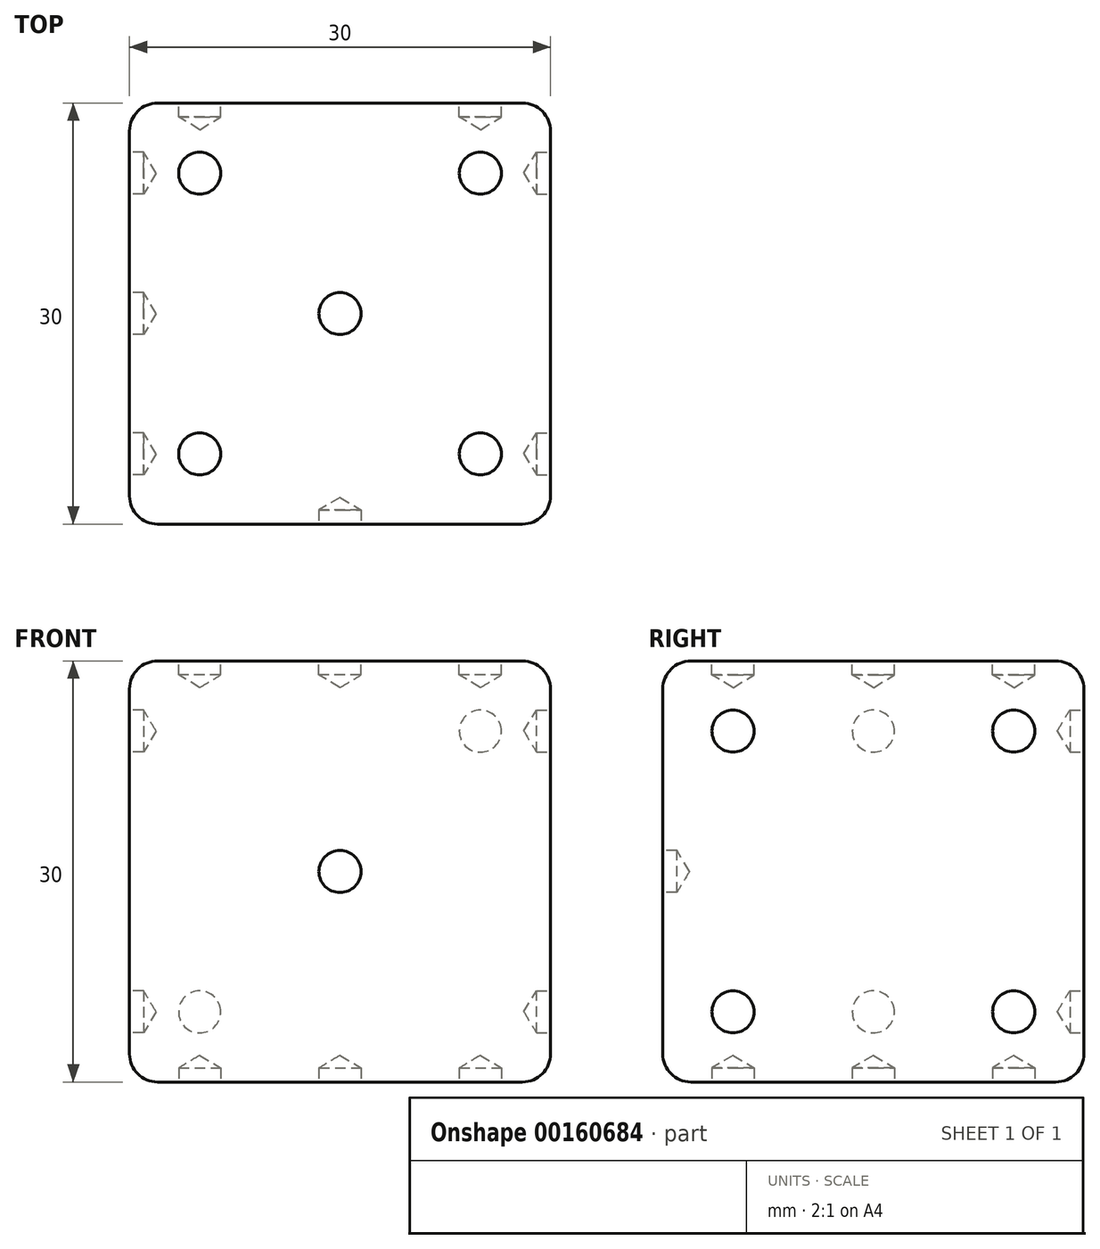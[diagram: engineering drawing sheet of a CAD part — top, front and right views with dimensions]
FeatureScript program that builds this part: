
annotation { "Feature Type Name" : "Feature", "Feature Type Description" : "" }
export const myFeature = defineFeature(function(context is Context, id is Id, definition is map)
    precondition{}
    {
        {
            var Q0;
            Q0=qCreatedBy(makeId("Front.planeOp"),FACE);
            var sketch = newSketch(context, id + "F0", { "sketchPlane" : qUnion([Q0])});
            skLineSegment(sketch, "E0.bottom", {"start": v(15, -15) * mm, "end": v(-15, -15) * mm});
            skLineSegment(sketch, "E0.top", {"start": v(15, 15) * mm, "end": v(-15, 15) * mm});
            skLineSegment(sketch, "E0.left", {"start": v(15, -15) * mm, "end": v(15, 15) * mm});
            skLineSegment(sketch, "E0.right", {"start": v(-15, -15) * mm, "end": v(-15, 15) * mm});
            skPoint(sketch, "E0.middle", {"position": v(0, 0) * mm});
            skSolve(sketch);
        }
        {
            var Q0;
            Q0=makeQuery(id+"F0.imprint","IMPRINT",FACE,{"disambiguationData":[TD([[makeQuery(id+"F0.imprint","IMPRINT",EDGE,{"derivedFrom":sQuery(id+"F0.wireOp",EDGE,"E0.bottom")}),-1.0]])]});
            extrude(context, id + "F1", {"entities" : qUnion([Q0]), "endBound" : BoundingType.SYMMETRIC, "depth" : 30 * mm});
        }
        {
            var Q0;
            Q0=makeQuery(id+"F1.opExtrude","CAP_EDGE",EDGE,{"disambiguationData":[OSD([sQuery(id+"F0.wireOp",EDGE,"E0.top")])],"isStart":false});
            var Q1;
            Q1=makeQuery(id+"F1.opExtrude","CAP_EDGE",EDGE,{"disambiguationData":[OSD([sQuery(id+"F0.wireOp",EDGE,"E0.left")])],"isStart":false});
            var Q2;
            Q2=makeQuery(id+"F1.opExtrude","SWEPT_EDGE",EDGE,{"disambiguationData":[OSD([sQuery(id+"F0.wireOp",EDGE,"E0.top"),sQuery(id+"F0.wireOp",EDGE,"E0.left")])]});
            var Q3;
            Q3=makeQuery(id+"F1.opExtrude","CAP_EDGE",EDGE,{"disambiguationData":[OSD([sQuery(id+"F0.wireOp",EDGE,"E0.top")])],"isStart":true});
            var Q4;
            Q4=makeQuery(id+"F1.opExtrude","SWEPT_EDGE",EDGE,{"disambiguationData":[OSD([sQuery(id+"F0.wireOp",EDGE,"E0.top"),sQuery(id+"F0.wireOp",EDGE,"E0.right")])]});
            var Q5;
            Q5=makeQuery(id+"F1.opExtrude","CAP_EDGE",EDGE,{"disambiguationData":[OSD([sQuery(id+"F0.wireOp",EDGE,"E0.left")])],"isStart":true});
            var Q6;
            Q6=makeQuery(id+"F1.opExtrude","SWEPT_EDGE",EDGE,{"disambiguationData":[OSD([sQuery(id+"F0.wireOp",EDGE,"E0.bottom"),sQuery(id+"F0.wireOp",EDGE,"E0.left")])]});
            var Q7;
            Q7=makeQuery(id+"F1.opExtrude","CAP_EDGE",EDGE,{"disambiguationData":[OSD([sQuery(id+"F0.wireOp",EDGE,"E0.bottom")])],"isStart":false});
            var Q8;
            Q8=makeQuery(id+"F1.opExtrude","CAP_EDGE",EDGE,{"disambiguationData":[OSD([sQuery(id+"F0.wireOp",EDGE,"E0.right")])],"isStart":false});
            var Q9;
            Q9=makeQuery(id+"F1.opExtrude","CAP_EDGE",EDGE,{"disambiguationData":[OSD([sQuery(id+"F0.wireOp",EDGE,"E0.right")])],"isStart":true});
            var Q10;
            Q10=makeQuery(id+"F1.opExtrude","SWEPT_EDGE",EDGE,{"disambiguationData":[OSD([sQuery(id+"F0.wireOp",EDGE,"E0.bottom"),sQuery(id+"F0.wireOp",EDGE,"E0.right")])]});
            var Q11;
            Q11=makeQuery(id+"F1.opExtrude","CAP_EDGE",EDGE,{"disambiguationData":[OSD([sQuery(id+"F0.wireOp",EDGE,"E0.bottom")])],"isStart":true});
            fillet(context, id + "F2", {"entities" : qUnion([Q0, Q1, Q2, Q3, Q4, Q5, Q6, Q7, Q8, Q9, Q10, Q11]), "radius" : 2 * mm, "tangentPropagation" : true, "allowEdgeOverflow" : false});
        }
        {
            var Q0;
            Q0=makeQuery(id+"F1.opExtrude","CAP_FACE",FACE,{"disambiguationData":[OSD([sQuery(id+"F0.wireOp",EDGE,"E0.bottom"),sQuery(id+"F0.wireOp",EDGE,"E0.top"),sQuery(id+"F0.wireOp",EDGE,"E0.left"),sQuery(id+"F0.wireOp",EDGE,"E0.right")])],"isStart":false});
            var sketch = newSketch(context, id + "F3", { "sketchPlane" : qUnion([Q0])});
            skPoint(sketch, "E1", {"position": v(0, 0) * mm});
            skSolve(sketch);
        }
        {
            var Q0;
            Q0=makeQuery(id+"F1.opExtrude","SWEPT_FACE",FACE,{"disambiguationData":[OSD([sQuery(id+"F0.wireOp",EDGE,"E0.bottom")])]});
            var sketch = newSketch(context, id + "F4", { "sketchPlane" : qUnion([Q0])});
            skPoint(sketch, "E2", {"position": v(10, 10) * mm});
            skPoint(sketch, "E3", {"position": v(0, 0) * mm});
            skPoint(sketch, "E4", {"position": v(-10, -10) * mm});
            skSolve(sketch);
        }
        {
            var Q0;
            Q0=makeQuery(id+"F1.opExtrude","SWEPT_FACE",FACE,{"disambiguationData":[OSD([sQuery(id+"F0.wireOp",EDGE,"E0.left")])]});
            var sketch = newSketch(context, id + "F5", { "sketchPlane" : qUnion([Q0])});
            skPoint(sketch, "E5", {"position": v(-10, 10) * mm});
            skPoint(sketch, "E6", {"position": v(-10, -10) * mm});
            skPoint(sketch, "E7", {"position": v(10, -10) * mm});
            skPoint(sketch, "E8", {"position": v(10, 10) * mm});
            skSolve(sketch);
        }
        {
            var Q0;
            Q0=makeQuery(id+"F1.opExtrude","CAP_FACE",FACE,{"disambiguationData":[OSD([sQuery(id+"F0.wireOp",EDGE,"E0.bottom"),sQuery(id+"F0.wireOp",EDGE,"E0.top"),sQuery(id+"F0.wireOp",EDGE,"E0.left"),sQuery(id+"F0.wireOp",EDGE,"E0.right")])],"isStart":true});
            var sketch = newSketch(context, id + "F6", { "sketchPlane" : qUnion([Q0])});
            skPoint(sketch, "E9", {"position": v(-10, 10) * mm});
            skPoint(sketch, "E10", {"position": v(10, -10) * mm});
            skSolve(sketch);
        }
        {
            var Q0;
            Q0=makeQuery(id+"F1.opExtrude","SWEPT_FACE",FACE,{"disambiguationData":[OSD([sQuery(id+"F0.wireOp",EDGE,"E0.top")])]});
            var sketch = newSketch(context, id + "F7", { "sketchPlane" : qUnion([Q0])});
            skPoint(sketch, "E11.middle", {"position": v(0, 0) * mm});
            skPoint(sketch, "E12", {"position": v(-10, -10) * mm});
            skPoint(sketch, "E13", {"position": v(-10, 10) * mm});
            skPoint(sketch, "E14", {"position": v(10, -10) * mm});
            skPoint(sketch, "E15", {"position": v(10, 10) * mm});
            skSolve(sketch);
        }
        {
            var Q0;
            Q0=makeQuery(id+"F1.opExtrude","SWEPT_FACE",FACE,{"disambiguationData":[OSD([sQuery(id+"F0.wireOp",EDGE,"E0.right")])]});
            var sketch = newSketch(context, id + "F8", { "sketchPlane" : qUnion([Q0])});
            skPoint(sketch, "E16", {"position": v(0, 10) * mm});
            skPoint(sketch, "E17", {"position": v(10, 10) * mm});
            skPoint(sketch, "E18", {"position": v(10, -10) * mm});
            skPoint(sketch, "E19", {"position": v(0, -10) * mm});
            skPoint(sketch, "E20", {"position": v(-10, -10) * mm});
            skPoint(sketch, "E21", {"position": v(-10, 10) * mm});
            skSolve(sketch);
        }
        {
            var Q0;
            Q0=sQuery(id+"F5.wireOp",VERTEX,"E5");
            var Q1;
            Q1=sQuery(id+"F5.wireOp",VERTEX,"E6");
            var Q2;
            Q2=sQuery(id+"F5.wireOp",VERTEX,"E8");
            var Q3;
            Q3=sQuery(id+"F5.wireOp",VERTEX,"E7");
            var Q4;
            Q4=sQuery(id+"F8.wireOp",VERTEX,"E19");
            var Q5;
            Q5=sQuery(id+"F8.wireOp",VERTEX,"E16");
            var Q6;
            Q6=sQuery(id+"F8.wireOp",VERTEX,"E17");
            var Q7;
            Q7=sQuery(id+"F8.wireOp",VERTEX,"E21");
            var Q8;
            Q8=sQuery(id+"F8.wireOp",VERTEX,"E18");
            var Q9;
            Q9=sQuery(id+"F8.wireOp",VERTEX,"E20");
            var Q10;
            Q10=sQuery(id+"F6.wireOp",VERTEX,"E10");
            var Q11;
            Q11=sQuery(id+"F6.wireOp",VERTEX,"E9");
            var Q12;
            Q12=sQuery(id+"F7.wireOp",VERTEX,"E15");
            var Q13;
            Q13=sQuery(id+"F7.wireOp",VERTEX,"E11.middle");
            var Q14;
            Q14=sQuery(id+"F7.wireOp",VERTEX,"E13");
            var Q15;
            Q15=sQuery(id+"F7.wireOp",VERTEX,"E14");
            var Q16;
            Q16=sQuery(id+"F7.wireOp",VERTEX,"E12");
            var Q17;
            Q17=sQuery(id+"F4.wireOp",VERTEX,"E4");
            var Q18;
            Q18=sQuery(id+"F4.wireOp",VERTEX,"E2");
            var Q19;
            Q19=sQuery(id+"F4.wireOp",VERTEX,"E3");
            var Q20;
            Q20=sQuery(id+"F3.wireOp",VERTEX,"E1");
            var Q21;
            Q21=makeQuery(id+"F1.opExtrude","SWEPT_BODY",BODY,{"disambiguationData":[OSD([sQuery(id+"F0.wireOp",EDGE,"E0.bottom"),sQuery(id+"F0.wireOp",EDGE,"E0.top"),sQuery(id+"F0.wireOp",EDGE,"E0.left"),sQuery(id+"F0.wireOp",EDGE,"E0.right")])]});
            hole(context, id + "F9", {"style" : HoleStyle.SIMPLE, "endStyle" : HoleEndStyle.BLIND, "holeDiameter" : 3 * mm, "holeDepth" : 1 * mm, "locations" : qUnion([Q0, Q1, Q2, Q3, Q4, Q5, Q6, Q7, Q8, Q9, Q10, Q11, Q12, Q13, Q14, Q15, Q16, Q17, Q18, Q19, Q20]), "scope" : qUnion([Q21])});
        }
    });
